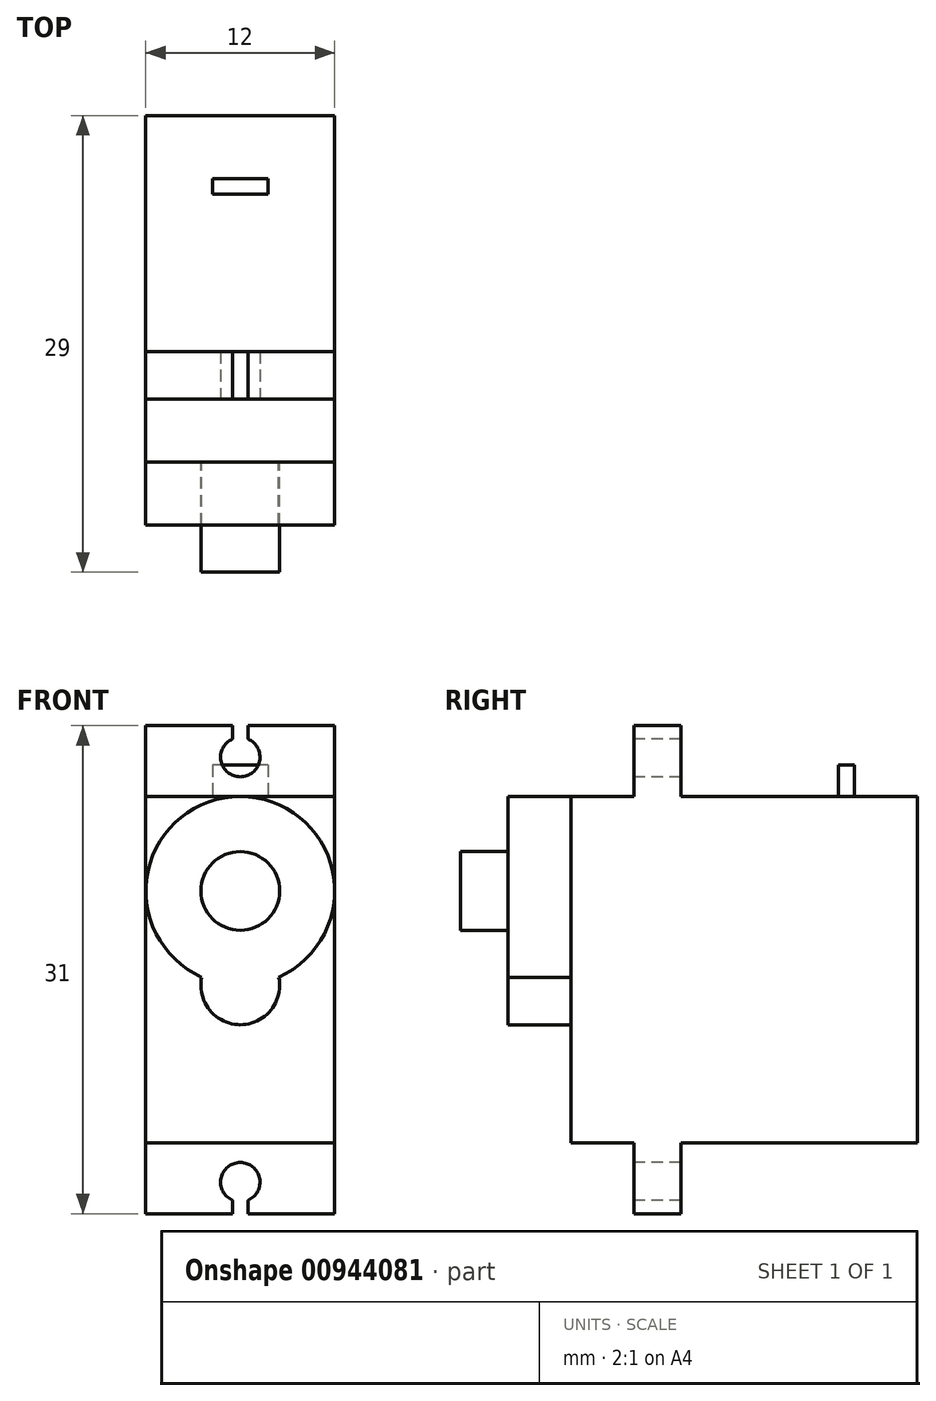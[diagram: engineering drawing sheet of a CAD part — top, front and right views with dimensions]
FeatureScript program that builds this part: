
annotation { "Feature Type Name" : "Feature", "Feature Type Description" : "" }
export const myFeature = defineFeature(function(context is Context, id is Id, definition is map)
    precondition{}
    {
        {
            var Q0;
            Q0=qCreatedBy(makeId("Front.planeOp"),FACE);
            var sketch = newSketch(context, id + "F0", { "sketchPlane" : qUnion([Q0])});
            skLineSegment(sketch, "E0.bottom", {"start": v(6, 11) * mm, "end": v(-6, 11) * mm});
            skLineSegment(sketch, "E0.top", {"start": v(6, -11) * mm, "end": v(-6, -11) * mm});
            skLineSegment(sketch, "E0.left", {"start": v(6, 11) * mm, "end": v(6, -11) * mm});
            skLineSegment(sketch, "E0.right", {"start": v(-6, 11) * mm, "end": v(-6, -11) * mm});
            skPoint(sketch, "E0.middle", {"position": v(0, 0) * mm});
            skSolve(sketch);
        }
        {
            var Q0;
            Q0 = qSketchRegion(id + "F0", true);
            var Q1;
            Q1=makeQuery(id+"F0.imprint","IMPRINT",FACE,{"disambiguationData":[TD([[makeQuery(id+"F0.imprint","IMPRINT",EDGE,{"derivedFrom":sQuery(id+"F0.wireOp",EDGE,"E0.bottom")}),1.0]])]});
            extrude(context, id + "F1", {"entities" : qUnion([Q0, Q1]), "oppositeDirection" : true, "depth" : 22 * mm, "offsetDistance" : 25.4 * mm});
        }
        {
            var Q0;
            Q0=makeQuery(id+"F1.opExtrude","CAP_FACE",FACE,{"disambiguationData":[OSD([sQuery(id+"F0.wireOp",EDGE,"E0.bottom"),sQuery(id+"F0.wireOp",EDGE,"E0.top"),sQuery(id+"F0.wireOp",EDGE,"E0.left"),sQuery(id+"F0.wireOp",EDGE,"E0.right")])],"isStart":true});
            var sketch = newSketch(context, id + "F2", { "sketchPlane" : qUnion([Q0])});
            skCircle(sketch, "E1", {"center": v(0, 5) * mm, "radius": 6 * mm});
            skCircle(sketch, "E2", {"center": v(0, -1) * mm, "radius": 2.5 * mm});
            skSolve(sketch);
        }
        {
            var Q0;
            Q0 = qSketchRegion(id + "F2", true);
            extrude(context, id + "F3", {"entities" : qUnion([Q0]), "operationType" : NewBodyOperationType.ADD, "depth" : 4 * mm, "offsetDistance" : 25 * mm});
        }
        {
            var Q0;
            Q0=makeQuery(id+"F3.opExtrude","CAP_FACE",FACE,{"disambiguationData":[OSD([sQuery(id+"F2.wireOp",EDGE,"E1"),sQuery(id+"F2.wireOp",EDGE,"E2")])],"isStart":false});
            var sketch = newSketch(context, id + "F4", { "sketchPlane" : qUnion([Q0])});
            skCircle(sketch, "E3", {"center": v(0, 5) * mm, "radius": 2.5 * mm});
            skSolve(sketch);
        }
        {
            var Q0;
            Q0 = qSketchRegion(id + "F4", true);
            extrude(context, id + "F5", {"entities" : qUnion([Q0]), "operationType" : NewBodyOperationType.ADD, "depth" : 3 * mm, "offsetDistance" : 25 * mm});
        }
        {
            var Q0;
            Q0=makeQuery(id+"F1.opExtrude","SWEPT_FACE",FACE,{"disambiguationData":[OSD([sQuery(id+"F0.wireOp",EDGE,"E0.bottom")])]});
            var sketch = newSketch(context, id + "F6", { "sketchPlane" : qUnion([Q0])});
            skLineSegment(sketch, "E4.bottom", {"start": v(6, 7) * mm, "end": v(-6, 7) * mm});
            skLineSegment(sketch, "E4.top", {"start": v(6, 4) * mm, "end": v(-6, 4) * mm});
            skLineSegment(sketch, "E4.left", {"start": v(6, 7) * mm, "end": v(6, 4) * mm});
            skLineSegment(sketch, "E4.right", {"start": v(-6, 7) * mm, "end": v(-6, 4) * mm});
            skPoint(sketch, "E4.middle", {"position": v(0, 5.5) * mm});
            skSolve(sketch);
        }
        {
            var Q0;
            Q0 = qSketchRegion(id + "F6", true);
            extrude(context, id + "F7", {"entities" : qUnion([Q0]), "operationType" : NewBodyOperationType.ADD, "depth" : 4.5 * mm, "offsetDistance" : 25 * mm});
        }
        {
            var Q0;
            Q0=makeQuery(id+"F1.opExtrude","SWEPT_FACE",FACE,{"disambiguationData":[OSD([sQuery(id+"F0.wireOp",EDGE,"E0.top")])]});
            var sketch = newSketch(context, id + "F8", { "sketchPlane" : qUnion([Q0])});
            skLineSegment(sketch, "E5.bottom", {"start": v(6, -7) * mm, "end": v(-6, -7) * mm});
            skLineSegment(sketch, "E5.top", {"start": v(6, -4) * mm, "end": v(-6, -4) * mm});
            skLineSegment(sketch, "E5.left", {"start": v(6, -7) * mm, "end": v(6, -4) * mm});
            skLineSegment(sketch, "E5.right", {"start": v(-6, -7) * mm, "end": v(-6, -4) * mm});
            skPoint(sketch, "E5.middle", {"position": v(0, -5.5) * mm});
            skSolve(sketch);
        }
        {
            var Q0;
            Q0 = qSketchRegion(id + "F8", true);
            extrude(context, id + "F9", {"entities" : qUnion([Q0]), "operationType" : NewBodyOperationType.ADD, "depth" : 4.5 * mm, "offsetDistance" : 25 * mm});
        }
        {
            var Q0;
            Q0=makeQuery(id+"F7.opExtrude","SWEPT_FACE",FACE,{"disambiguationData":[OSD([sQuery(id+"F6.wireOp",EDGE,"E4.top")])]});
            var sketch = newSketch(context, id + "F10", { "sketchPlane" : qUnion([Q0])});
            skCircle(sketch, "E6", {"center": v(0, 13.5) * mm, "radius": 1.25 * mm});
            skLineSegment(sketch, "E7", {"start": v(0.5, 14.65) * mm, "end": v(0.5, 15.5) * mm});
            skLineSegment(sketch, "E8", {"start": v(0, 13.5) * mm, "end": v(0, 15.5) * mm, "construction": true});
            skLineSegment(sketch, "E9.MirrorCS", {"start": v(-0.5, 14.65) * mm, "end": v(-0.5, 15.5) * mm});
            skLineSegment(sketch, "E10", {"start": v(-0.5, 15.5) * mm, "end": v(0.5, 15.5) * mm});
            skSolve(sketch);
        }
        {
            var Q0;
            Q0 = qSketchRegion(id + "F10", true);
            var Q1;
            Q1=makeQuery(id+"F7.opExtrude","SWEPT_FACE",FACE,{"disambiguationData":[OSD([sQuery(id+"F6.wireOp",EDGE,"E4.bottom")])]});
            extrude(context, id + "F11", {"entities" : qUnion([Q0]), "operationType" : NewBodyOperationType.REMOVE, "endBound" : BoundingType.UP_TO_SURFACE, "oppositeDirection" : true, "depth" : 25 * mm, "endBoundEntityFace" : qUnion([Q1]), "offsetDistance" : 25 * mm});
        }
        {
            var Q0;
            Q0=makeQuery(id+"F9.opExtrude","SWEPT_FACE",FACE,{"disambiguationData":[OSD([sQuery(id+"F8.wireOp",EDGE,"E5.top")])]});
            var sketch = newSketch(context, id + "F12", { "sketchPlane" : qUnion([Q0])});
            skCircle(sketch, "E11", {"center": v(0, -13.5) * mm, "radius": 1.25 * mm});
            skPoint(sketch, "E11.centerSnap0", {"position": v(0, -15.5) * mm});
            skLineSegment(sketch, "E12", {"start": v(0, -13.5) * mm, "end": v(0, -15.5) * mm, "construction": true});
            skLineSegment(sketch, "E13", {"start": v(-0.5, -14.65) * mm, "end": v(-0.5, -15.5) * mm});
            skLineSegment(sketch, "E14.MirrorCS", {"start": v(0.5, -14.65) * mm, "end": v(0.5, -15.5) * mm});
            skLineSegment(sketch, "E15", {"start": v(-0.5, -15.5) * mm, "end": v(0.5, -15.5) * mm});
            skSolve(sketch);
        }
        {
            var Q0;
            Q0 = qSketchRegion(id + "F12", true);
            var Q1;
            Q1=makeQuery(id+"F9.opExtrude","SWEPT_FACE",FACE,{"disambiguationData":[OSD([sQuery(id+"F8.wireOp",EDGE,"E5.bottom")])]});
            extrude(context, id + "F13", {"entities" : qUnion([Q0]), "operationType" : NewBodyOperationType.REMOVE, "endBound" : BoundingType.UP_TO_SURFACE, "oppositeDirection" : true, "depth" : 25 * mm, "endBoundEntityFace" : qUnion([Q1]), "offsetDistance" : 25 * mm});
        }
        {
            var Q0;
            {var subQ2=sQuery(id+"F0.wireOp",EDGE,"E0.bottom");Q0=makeQuery(id+"F7.boolean.opBoolean","SPLIT",FACE,{"disambiguationData":[TD([makeQuery(id+"F7.opExtrude","SWEPT_FACE",FACE,{"disambiguationData":[OSD([sQuery(id+"F6.wireOp",EDGE,"E4.bottom")])]})])],"derivedFrom":makeQuery(id+"F1.opExtrude","SWEPT_FACE",FACE,{"disambiguationData":[OSD([subQ2])]})});}
            var sketch = newSketch(context, id + "F14", { "sketchPlane" : qUnion([Q0])});
            skLineSegment(sketch, "E16.bottom", {"start": v(1.75, 18) * mm, "end": v(-1.75, 18) * mm});
            skLineSegment(sketch, "E16.top", {"start": v(1.75, 17) * mm, "end": v(-1.75, 17) * mm});
            skLineSegment(sketch, "E16.left", {"start": v(1.75, 18) * mm, "end": v(1.75, 17) * mm});
            skLineSegment(sketch, "E16.right", {"start": v(-1.75, 18) * mm, "end": v(-1.75, 17) * mm});
            skPoint(sketch, "E16.middle", {"position": v(0, 17.5) * mm});
            skSolve(sketch);
        }
        {
            var Q0;
            Q0 = qSketchRegion(id + "F14", true);
            extrude(context, id + "F15", {"entities" : qUnion([Q0]), "operationType" : NewBodyOperationType.ADD, "depth" : 2 * mm, "offsetDistance" : 25 * mm});
        }
    });
